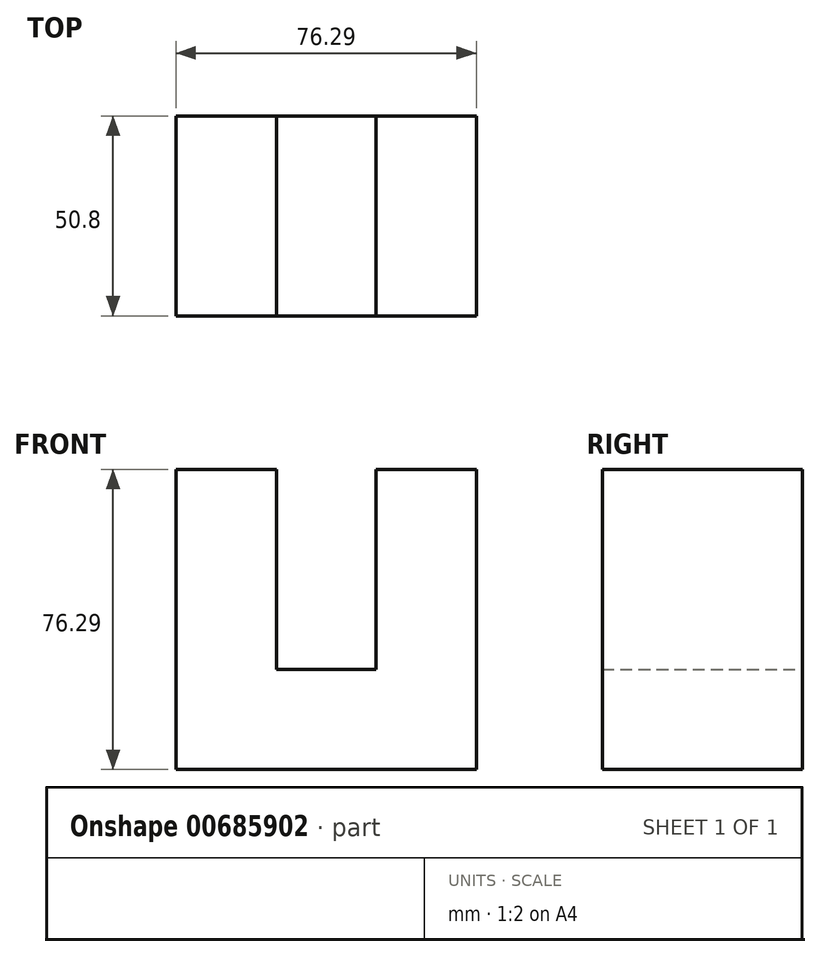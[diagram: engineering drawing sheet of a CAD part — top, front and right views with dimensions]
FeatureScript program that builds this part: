
annotation { "Feature Type Name" : "Feature", "Feature Type Description" : "" }
export const myFeature = defineFeature(function(context is Context, id is Id, definition is map)
    precondition{}
    {
        {
            var Q0;
            Q0=qCreatedBy(makeId("Front.planeOp"),FACE);
            var sketch = newSketch(context, id + "F0", { "sketchPlane" : qUnion([Q0])});
            skLineSegment(sketch, "E0", {"start": v(0, 0) * mm, "end": v(-76.29, 0) * mm});
            skLineSegment(sketch, "E1", {"start": v(-76.29, 0) * mm, "end": v(-76.29, 76.29) * mm});
            skLineSegment(sketch, "E2", {"start": v(0, 0) * mm, "end": v(0, 76.29) * mm});
            skLineSegment(sketch, "E3", {"start": v(0, 76.29) * mm, "end": v(-25.5, 76.29) * mm});
            skLineSegment(sketch, "E4", {"start": v(-76.29, 76.29) * mm, "end": v(-50.7, 76.29) * mm});
            skLineSegment(sketch, "E5", {"start": v(-50.7, 76.29) * mm, "end": v(-50.7, 25.5) * mm});
            skLineSegment(sketch, "E6", {"start": v(-25.5, 76.29) * mm, "end": v(-25.5, 25.5) * mm});
            skLineSegment(sketch, "E7", {"start": v(-25.5, 25.5) * mm, "end": v(-50.7, 25.5) * mm});
            skSolve(sketch);
        }
        {
            var Q0;
            Q0 = qSketchRegion(id + "F0", true);
            extrude(context, id + "F1", {"entities" : qUnion([Q0]), "depth" : 50.8 * mm, "offsetDistance" : 25.4 * mm});
        }
    });
